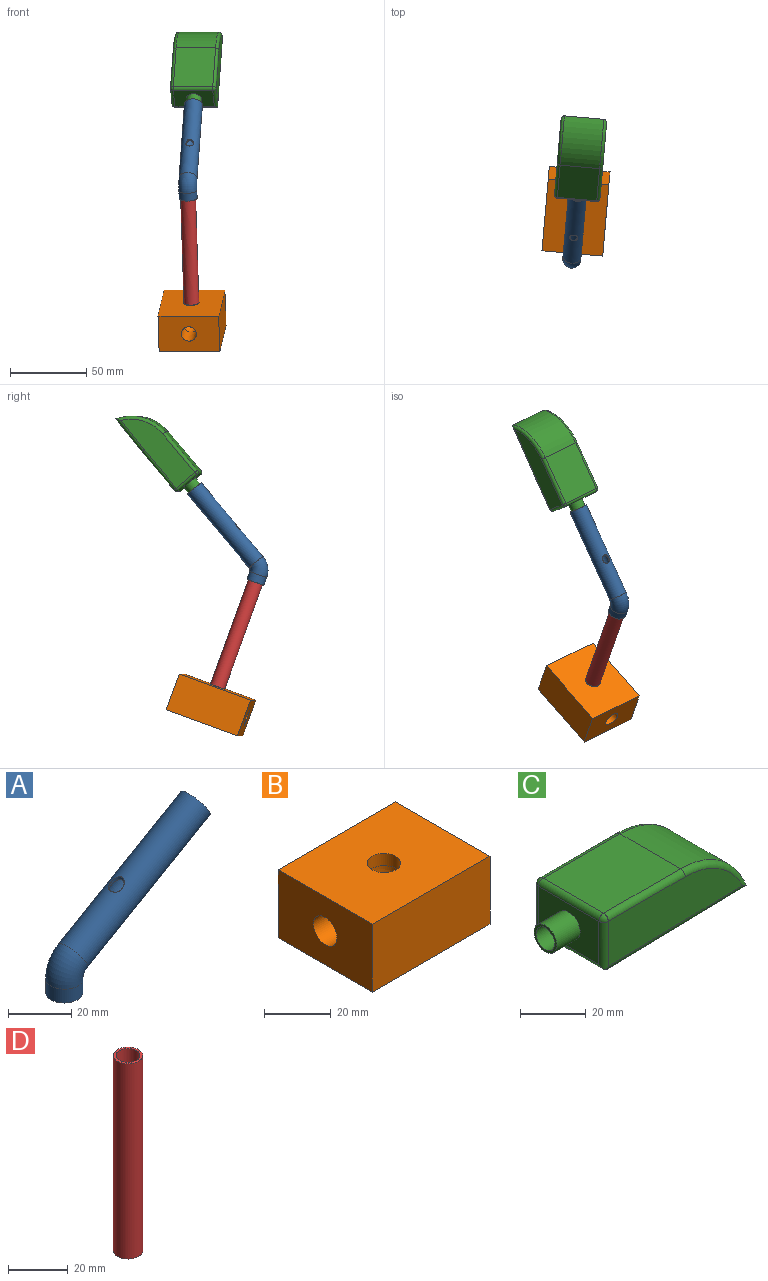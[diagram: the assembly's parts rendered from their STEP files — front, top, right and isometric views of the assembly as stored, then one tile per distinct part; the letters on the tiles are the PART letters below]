
ASSEMBLY  parts=4 mates=3
PART A: 9 faces, bbox 68.8x11.8x49 mm
  f0: cylinder r=5mm len=59.77mm, axis (0.87,0,0.5), area 1963.2mm2, adj f3,f5,f8
  f1: cylinder r=5.9mm len=60.67mm, axis (0.87,0,0.5), area 2321.1mm2, adj f5,f7,f8
  f2: cylinder r=5mm len=10mm, axis (0,0,1), area 169.1mm2, adj f3,f4
  f3: torus R=8mm, axis (0,1,0), area 263.2mm2, adj f0,f2
  f4: plane 11.8x11.8mm, normal (0,0,-1), area 30.8mm2, adj f2,f6
  f5: plane 11.8x10.22mm, normal (0.87,0,0.5), area 30.8mm2, adj f0,f1
  f6: cylinder r=5.9mm len=11.8mm, axis (0,0,1), area 199.5mm2, adj f4,f7
  f7: torus R=8mm, axis (0,1,0), area 310.6mm2, adj f1,f6
  f8: cylinder r=2.5mm len=5mm, axis (0,0,-1), area 17.3mm2, adj f0,f1
PART B: 9 faces, bbox 50x40x25 mm
  f0: plane 50x25mm, normal (0,1,0), area 1250mm2, adj f1,f3,f4,f5
  f1: plane 40x25mm, normal (-1,0,0), area 921.5mm2, adj f0,f2,f4,f5,f6
  f2: plane 50x25mm, normal (0,-1,0), area 1250mm2, adj f1,f3,f4,f5
  f3: plane 40x25mm, normal (1,0,0), area 1000mm2, adj f0,f2,f4,f5
  f4: plane 50x40mm, normal (0,0,1), area 1921.5mm2, adj f0,f1,f2,f3,f7
  f5: plane 50x40mm, normal (0,0,-1), area 2000mm2, adj f0,f1,f2,f3
  f6: cylinder r=5mm len=17mm, axis (-1,0,0), area 534.1mm2, adj f1,f8
  f7: cylinder r=5mm len=10mm, axis (0,0,-1), area 141.4mm2, adj f4,f8
  f8: torus R=8mm, axis (0,1,0), area 394.8mm2, adj f6,f7
PART C: 30 faces, bbox 74.8x30x23.2 mm
  f0: plane 33x27.58mm, normal (0,0,-1), area 94.3mm2, adj f1,f11,f12,f14,f19,f24,f27
  f1: plane 27.49x26mm, normal (0.02,0,-1), area 101.2mm2, adj f0,f4,f10,f11,f12,f17,f27
  f2: plane 33x26mm, normal (0,0,1), area 858mm2, adj f4,f18,f23,f28
  f3: plane 26x16mm, normal (-1,0,0), area 340.6mm2, adj f8,f20,f23,f24,f25
  f4: cylinder r=29.19mm len=27.49mm, axis (0,1,0), area 931.5mm2, adj f1,f2,f16,f29
  f5: plane 57.52x16.77mm, normal (0,-1,0), area 818.8mm2, adj f25,f27,f28,f29
  f6: plane 57.52x16mm, normal (0,1,0), area 806.1mm2, adj f16,f17,f18,f19,f20
  f7: cylinder r=4mm len=13mm, axis (1,0,0), area 326.7mm2, adj f9,f14
  f8: cylinder r=4.9mm len=10mm, axis (1,0,0), area 307.9mm2, adj f3,f9
  f9: plane 9.8x9.8mm, normal (-1,0,0), area 25.2mm2, adj f7,f8
  f10: plane 25x2.96mm, normal (-0.87,0,-0.49), area 84.7mm2, adj f1,f11,f12,f15
  f11: plane 56.54x17mm, normal (0,-1,0), area 840.4mm2, adj f0,f1,f10,f13,f14,f15
  f12: plane 56.54x17mm, normal (0,1,0), area 840.4mm2, adj f0,f1,f10,f13,f14,f15
  f13: plane 32x25mm, normal (0,0,-1), area 800mm2, adj f11,f12,f14,f15
  f14: plane 25x17mm, normal (1,0,0), area 374.7mm2, adj f0,f7,f11,f12,f13
  f15: cylinder r=26.19mm len=25mm, axis (0,-1,0), area 696.3mm2, adj f10,f11,f12,f13
  f16: torus R=27.19mm, axis (0,-1,0), area 106.6mm2, adj f4,f6,f17,f18
  f17: cylinder r=2mm len=27.53mm, axis (1,0,0.02), area 83.1mm2, adj f1,f6,f16,f19
  f18: cylinder r=2mm len=33mm, axis (-1,0,0), area 103.7mm2, adj f2,f6,f16,f21
  f19: cylinder r=2mm len=33mm, axis (1,0,0), area 103.6mm2, adj f0,f6,f17,f22
  f20: cylinder r=2mm len=16mm, axis (0,0,-1), area 50.3mm2, adj f3,f6,f21,f22
  f21: sphere r=2mm, area 6.3mm2, adj f18,f20,f23
  f22: sphere r=2mm, area 6.3mm2, adj f19,f20,f24
  f23: cylinder r=2mm len=26mm, axis (0,-1,0), area 81.7mm2, adj f2,f3,f21,f26
  f24: cylinder r=2mm len=27.75mm, axis (0,1,0), area 85.4mm2, adj f0,f3,f22,f25,f27
  f25: cylinder r=2mm len=17.75mm, axis (0,0,1), area 53.6mm2, adj f3,f5,f24,f26,f27
  f26: sphere r=2mm, area 6.3mm2, adj f23,f25,f28
  f27: cylinder r=2mm len=61.47mm, axis (-1,0,-0.02), area 148mm2, adj f0,f1,f5,f24,f25,f29
  f28: cylinder r=2mm len=33mm, axis (1,0,0), area 103.7mm2, adj f2,f5,f26,f29
  f29: torus R=27.19mm, axis (0,-1,0), area 106.6mm2, adj f4,f5,f27,f28
PART D: 4 faces, bbox 9.8x9.8x80 mm
  f0: cylinder r=4mm len=80mm, axis (0,0,-1), area 2010.6mm2, adj f2,f3
  f1: cylinder r=4.9mm len=80mm, axis (0,0,-1), area 2463mm2, adj f2,f3
  f2: plane 9.8x9.8mm, normal (0,0,1), area 25.2mm2, adj f0,f1
  f3: plane 9.8x9.8mm, normal (0,0,-1), area 25.2mm2, adj f0,f1
PLACE A rot(axis=(0.17,-0.19,0.97),86.9deg) t=(-22.47,18.87,80.79)mm
PLACE B rot(axis=(0.17,-0.19,0.97),86.9deg) t=(-19.91,48.13,0.08)mm
PLACE C rot(axis=(0.38,-0.42,0.82),96.1deg) t=(-18.68,62.2,146.1)mm
PLACE D rot(axis=(0.17,-0.19,0.97),86.9deg) t=(-20.3,43.74,12.19)mm
MATE slider D.f0 <-> B.f7  axis (0.03,0.34,-0.94) through (-20.3,43.74,12.19)mm
MATE slider C.f7 <-> A.f0  axis (-0.06,-0.64,-0.77) through (-19.24,55.79,138.44)mm
MATE slider A.f2 <-> D.f0  axis (-0.03,-0.34,0.94) through (-22.63,17.04,85.85)mm
